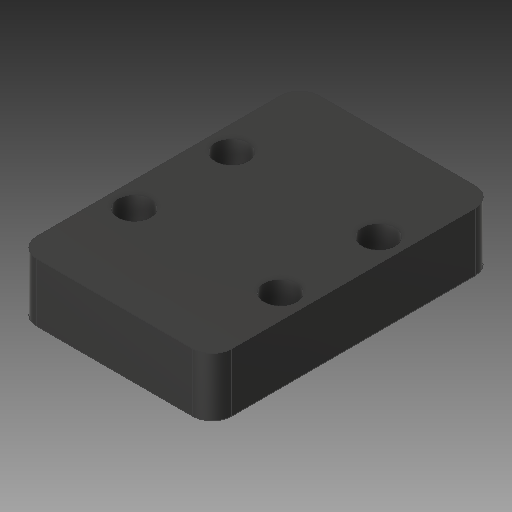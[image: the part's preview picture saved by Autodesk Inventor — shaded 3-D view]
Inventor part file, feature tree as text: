
AUTODESK INVENTOR PART (.ipt)
format: ipt  version: 2019 (Build 230136000, 136)  size: 115,200 bytes
history: native  units: mm
features: extrude x1, fillet x1, sketch x1
ambient origin geometry x8: Origin, YZ Plane, XZ Plane, XY Plane, X Axis, Y Axis, Z Axis, Center Point
bodies: Solid1 (feature_tree)
feature tree (3):
  extrude  "Extrusion1"  Depth=20.0mm
  fillet  "Fillet1"  Radius=15.0mm
  sketch  "Sketch1"  dims[d0=29.0mm d1=20.0mm d2=15.0mm d3=10.0mm d4=3.4mm d5=6.0mm d6=0.0mm d7=2.0mm]
